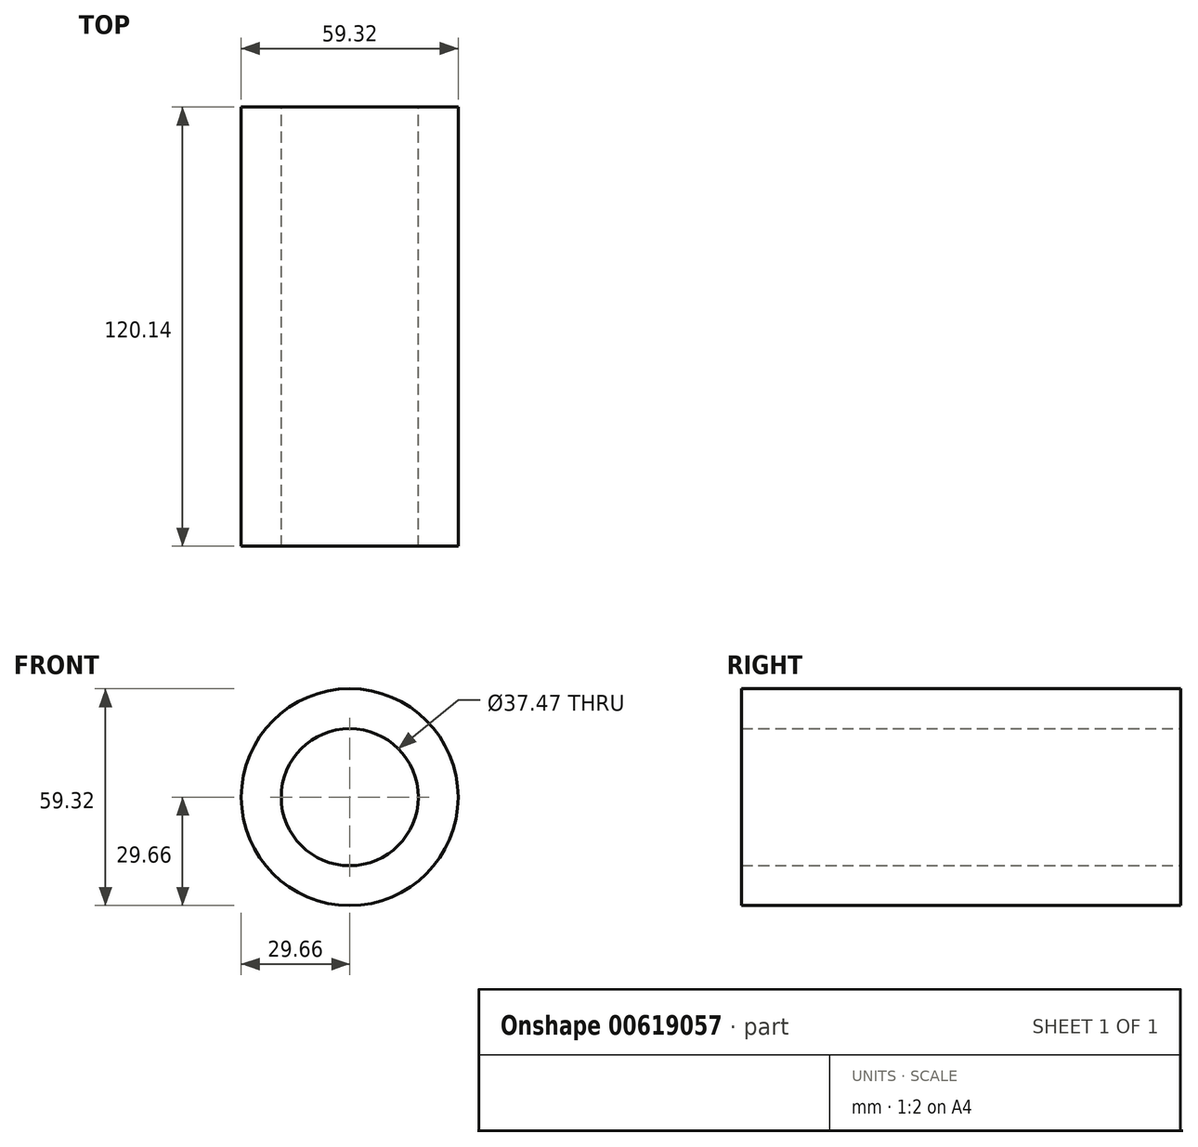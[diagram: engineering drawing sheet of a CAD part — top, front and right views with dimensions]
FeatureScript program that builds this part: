
annotation { "Feature Type Name" : "Feature", "Feature Type Description" : "" }
export const myFeature = defineFeature(function(context is Context, id is Id, definition is map)
    precondition{}
    {
        {
            var Q0;
            Q0=qCreatedBy(makeId("Front.planeOp"),FACE);
            var sketch = newSketch(context, id + "F0", { "sketchPlane" : qUnion([Q0])});
            skCircle(sketch, "E0", {"center": v(0, 0) * mm, "radius": 29.66 * mm});
            skCircle(sketch, "E1", {"center": v(0, 0) * mm, "radius": 18.74 * mm});
            skSolve(sketch);
        }
        {
            var Q0;
            Q0 = qSketchRegion(id + "F0", true);
            extrude(context, id + "F1", {"entities" : qUnion([Q0]), "depth" : 120.14 * mm, "offsetDistance" : 25.4 * mm});
        }
    });
